# Revit family: 71785XXX_NEW
name_source: partatom
category: Plumbing Fixtures
revit_build: Autodesk Revit 2018 (Build: 20170223_1515(x64)
units: mm (PartAtom-declared; Revit-internal decimal feet)

## family parameters
Always vertical = No
Cut with Voids When Loaded = No
OmniClass Number = 23.45.00.00
OmniClass Title = Sanitary, Laundry, and Cleaning Equipment
Part Type = Normal
Room Calculation Point = No
Round Connector Dimension = Use Diameter
Shared = No
Work Plane-Based = Yes

## types (1)
- 000 Chrome
    Always visible = Yes
    BIMobject category = Sanitary Taps & Mixers
    Default Elevation = 1219.2 mm  [stored 4 ft]
    Design country = Germany
    EAN code = 4059625334157
    Edition number = 1
    GTIN code = https://4059625334157
    IFC Classification = Sanitary Terminal
    Installation instructions = https://www.hansgrohe.com
    Manufacturer country = Germany
    Manufacturer name = hansgrohe
    Masterformat 2014 Code = 41 14 33
    Masterformat 2014 Description = Mixers
    Material 1 = Hansgrohe - Metal - 000 Chrome
    Material secondary = Chrome
    NBS Reference Code = 35-06-82
    NBS Reference Description = Shower Mixers
    Product Guid = 8316a35f-089f-4545-b2fb-011bad48bccc
    Product SKU = 71785XXX
    Product data url = https://www.bimobject.com
    Product family = Talis E
    Product group = Basin mixers
    Product name = 71785XXX Talis E Single lever basin mixer 80 without waste set Finland
    Product url = https://www.hansgrohe.com
    QR code = https://www.bimobject.com
    Technical description = https://www.hansgrohe.com
    Uniclass 2.0 Code = PR-35-06-82
    Uniclass 2.0 Description = Shower Mixers
    Uniclass 2015 Code = Pr_60_75_08_54
    Uniclass 2015 Name = Mixers
    Weight Net (Kg) = 1,3

note: [stored X ft] marks values corroborated as IEEE doubles in the binary element streams (Revit-internal decimal feet)

## geometry (parser evidence)
native form markers: Sweep x1
no freeform markers — native parametric forms only
